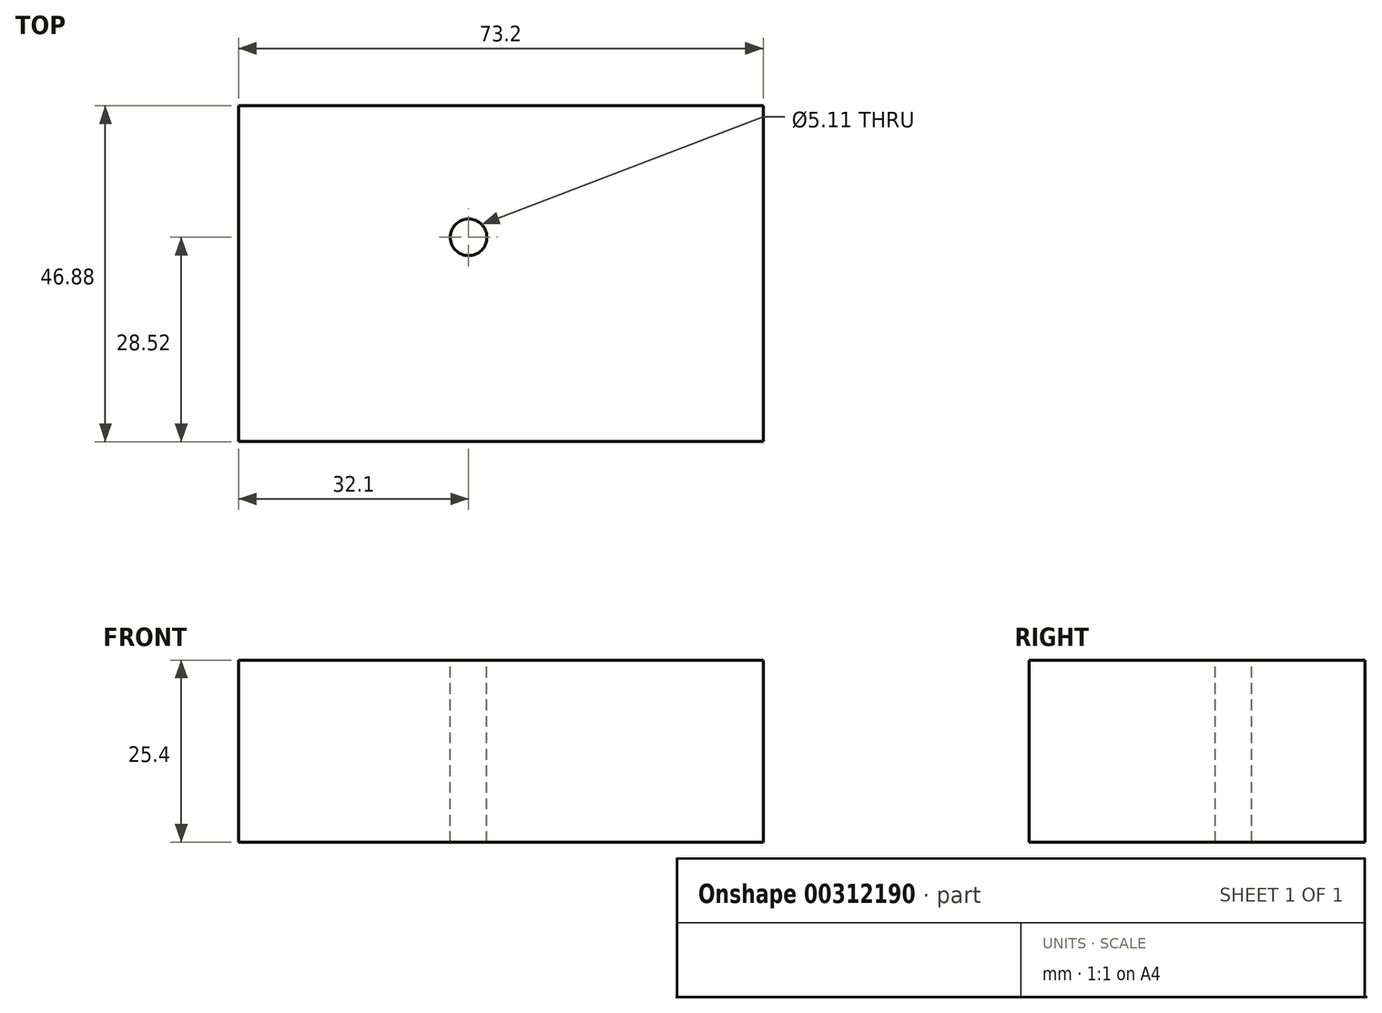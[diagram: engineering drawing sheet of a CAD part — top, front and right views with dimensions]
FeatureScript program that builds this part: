
annotation { "Feature Type Name" : "Feature", "Feature Type Description" : "" }
export const myFeature = defineFeature(function(context is Context, id is Id, definition is map)
    precondition{}
    {
        {
            var Q0;
            Q0=qCreatedBy(makeId("Top.planeOp"),FACE);
            var sketch = newSketch(context, id + "F0", { "sketchPlane" : qUnion([Q0])});
            skLineSegment(sketch, "E0.bottom", {"start": v(-32.1, 18.36) * mm, "end": v(41.1, 18.36) * mm});
            skLineSegment(sketch, "E0.top", {"start": v(-32.1, -28.52) * mm, "end": v(41.1, -28.52) * mm});
            skLineSegment(sketch, "E0.left", {"start": v(-32.1, 18.36) * mm, "end": v(-32.1, -28.52) * mm});
            skLineSegment(sketch, "E0.right", {"start": v(41.1, 18.36) * mm, "end": v(41.1, -28.52) * mm});
            skSolve(sketch);
        }
        {
            var Q0;
            Q0=makeQuery(id+"F0.imprint","IMPRINT",FACE,{"disambiguationData":[TD([[makeQuery(id+"F0.imprint","IMPRINT",EDGE,{"derivedFrom":sQuery(id+"F0.wireOp",EDGE,"E0.bottom")}),-1.0]])]});
            extrude(context, id + "F1", {"entities" : qUnion([Q0]), "depth" : 25.4 * mm});
        }
        {
            var Q0;
            Q0=makeQuery(id+"F1.opExtrude","CAP_FACE",FACE,{"disambiguationData":[OSD([sQuery(id+"F0.wireOp",EDGE,"E0.bottom"),sQuery(id+"F0.wireOp",EDGE,"E0.top"),sQuery(id+"F0.wireOp",EDGE,"E0.left"),sQuery(id+"F0.wireOp",EDGE,"E0.right")])],"isStart":false});
            var sketch = newSketch(context, id + "F2", { "sketchPlane" : qUnion([Q0])});
            skPoint(sketch, "E1", {"position": v(0, 0) * mm});
            skSolve(sketch);
        }
        {
            var Q0;
            Q0=sQuery(id+"F2.wireOp",VERTEX,"E1");
            var Q1;
            Q1=makeQuery(id+"F1.opExtrude","SWEPT_BODY",BODY,{"disambiguationData":[OSD([sQuery(id+"F0.wireOp",EDGE,"E0.bottom"),sQuery(id+"F0.wireOp",EDGE,"E0.top"),sQuery(id+"F0.wireOp",EDGE,"E0.left"),sQuery(id+"F0.wireOp",EDGE,"E0.right")])]});
            hole(context, id + "F3", {"style" : HoleStyle.SIMPLE, "endStyle" : HoleEndStyle.THROUGH, "standardTappedOrClearance" : lookupTablePath({ "standard" : "ANSI", "engagement" : "75%", "pitch" : "20 tpi", "size" : "1/4", "type" : "Tapped" }), "standardBlindInLast" : lookupTablePath({ "standard" : "ANSI", "engagement" : "75%", "pitch" : "20 tpi", "size" : "1/4", "type" : "Tapped" }), "holeDiameter" : 5.1 * mm, "showTappedDepth" : true, "tappedDepth" : 25.4 * mm, "tapClearance" : 3, "locations" : qUnion([Q0]), "scope" : qUnion([Q1]), "majorDiameter" : 6.35 * mm});
        }
    });
